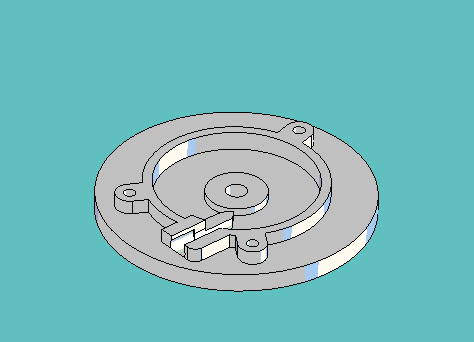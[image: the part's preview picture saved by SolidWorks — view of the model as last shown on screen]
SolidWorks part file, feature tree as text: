
SOLIDWORKS PART (.sldprt)
format: sldprt  version: not decoded by parser v0  size: 747,520 bytes
history: native  units: mm
features: sketch x12, extrude x9, cut_extrude x3, fillet x2, plane x2, material x1, chamfer x1 (+11 scaffold rows collapsed)
feature tree (41):
  scaffold x11  (default folders/planes/origin — collapsed)
  material  "Material <not specified>"
  sketch  "Sketch1"  dims[D1=~7.14375mm D2=60.325mm]
  extrude  "Extrude1"  Depth=4.7625mm
  sketch  "Sketch2"  dims[D1=3.175mm]
  extrude  "Extrude2"  Depth=2.286mm
  sketch  "Sketch3"  dims[c1.D4=7.9375mm c1.D1=~17.512839mm c2.D1=45.0deg c2.D2=~14.559872mm c2.D3=4.7625mm c2.D5=19.05mm]
  extrude  "Extrude3"  [1 undecoded]
  sketch  "Sketch4"  dims[D1=6.35mm]
  cut_extrude  "Cut-Extrude1"  [1 undecoded]
  sketch  "Sketch5"  dims[D2=~0.983272mm D1=0.0mm]
  extrude  "Extrude4"  Depth=4.16052mm
  sketch  "Sketch7"  dims[D1=4.7625mm D2=4.7625mm D3=6.35mm]
  extrude  "Extrude6"  [1 undecoded]
  sketch  "Sketch8"
  extrude  "Extrude7"  [1 undecoded]
  fillet  "Fillet1"  Radius=3.175mm
  sketch  "Sketch9"  dims[D1=~7.14375mm]
  cut_extrude  "Cut-Extrude2"  Depth=9.525mm
  sketch  "Sketch10"  dims[c1.D3=~3.96875mm c1.D6=~3.96875mm c1.D9=~3.96875mm c1.D1=4.7625mm c1.D2=4.7625mm c1.D4=~69.703815mm c2.D4=120.0deg c2.D5=4.7625mm c2.D6=4.7625mm c2.D7=~69.703815mm c3.D7=120.0deg c3.D8=4.7625mm c4.D7=~49.394425mm c5.D7=120.0deg c5.D4=~49.394425mm c6.D4=60.0deg c6.D7=~46.980774mm c7.D7=77.0deg c7.D10=~49.394425mm c8.D10=120.0deg c8.D1=~107.458775mm c9.D1=163.0deg c9.D2=4.7625mm c9.D10=~49.394425mm c10.D10=137.0deg c10.D11=~49.394425mm c11.D11=137.0deg]
  extrude  "Extrude8"  [1 undecoded]
  plane  "Plane1"
  sketch  "Sketch11"  dims[D1=20.32mm]
  extrude  "Extrude9"  Depth=2.667mm
  chamfer  "Chamfer1"  Distance=1.5875mm Angle=45deg
  sketch  "Sketch12"  dims[D2=2.7051mm D1=9.525mm]
  cut_extrude  "Cut-Extrude3"  [1 undecoded]
  plane  "Plane2"
  fillet  "Fillet2"  Radius=3.175mm
  sketch  "Sketch13"  dims[D2=90.3732mm D1=0.0mm]
  extrude  "Extrude10"  Depth=6.35mm
decode coverage: 20 of 27 modeling features carry decoded parameters
note: ~ marks probable driven/reference dimensions
note: 6 parameter values undecoded
summary: no parameter record found for 6 features
note: suppression state not decoded; provenance and decode notes live in map.json
